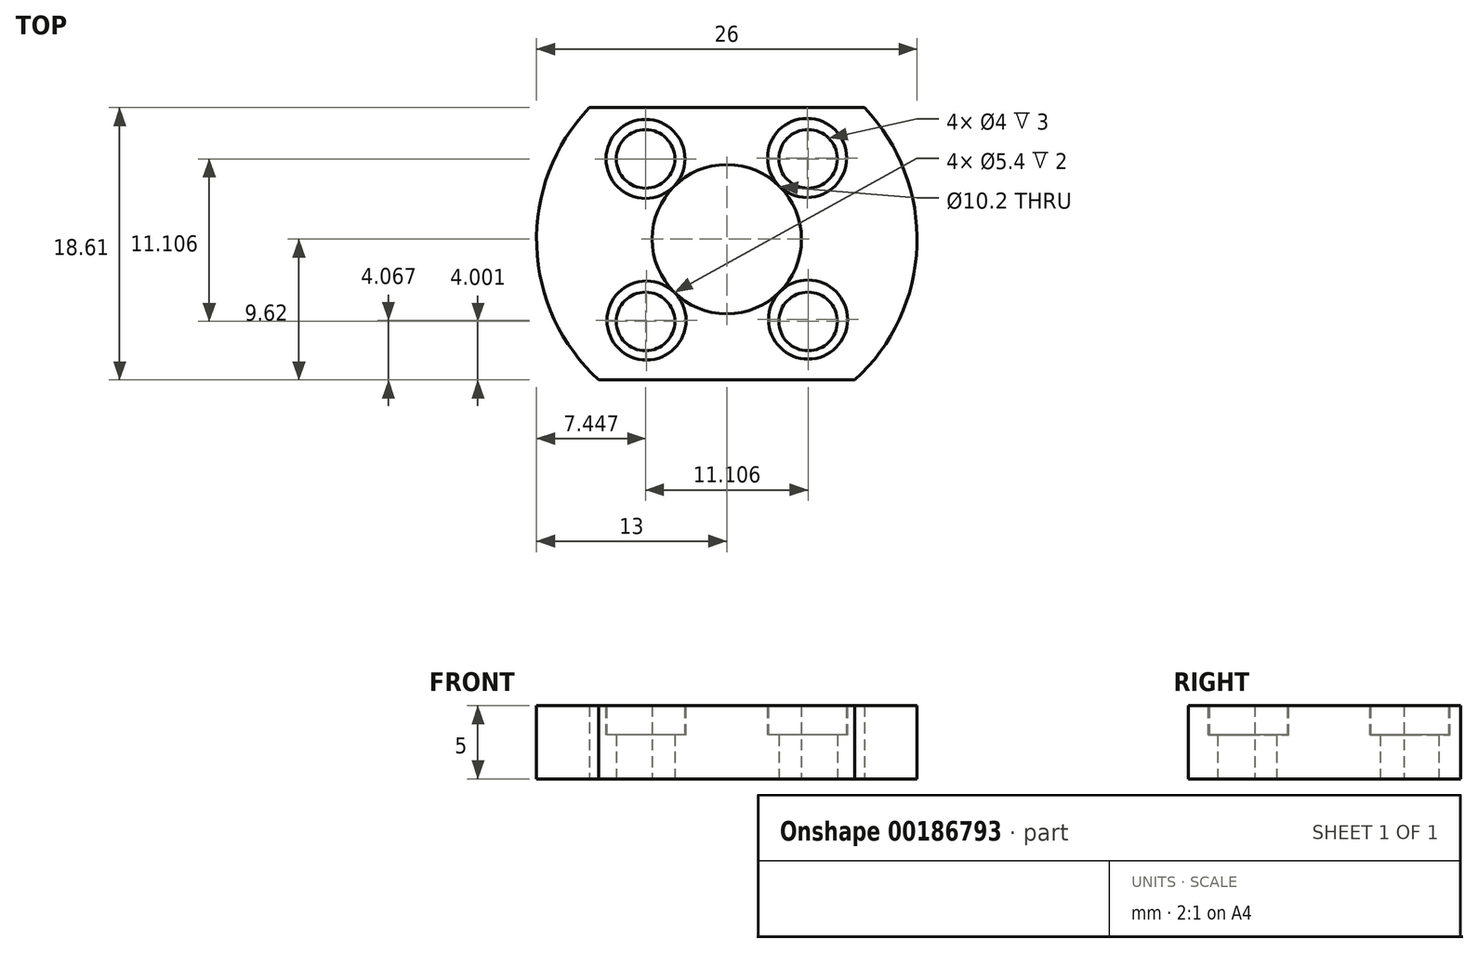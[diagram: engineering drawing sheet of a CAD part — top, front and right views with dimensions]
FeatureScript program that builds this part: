
annotation { "Feature Type Name" : "Feature", "Feature Type Description" : "" }
export const myFeature = defineFeature(function(context is Context, id is Id, definition is map)
    precondition{}
    {
        {
            var Q0;
            Q0=qCreatedBy(makeId("Top.planeOp"),FACE);
            var sketch = newSketch(context, id + "F0", { "sketchPlane" : qUnion([Q0])});
            skCircle(sketch, "E0", {"center": v(0, 0) * mm, "radius": 5.1 * mm});
            skCircle(sketch, "E1", {"center": v(-5.55, -5.62) * mm, "radius": 2 * mm});
            skCircle(sketch, "E2.1.0", {"center": v(5.55, -5.62) * mm, "radius": 2 * mm});
            skCircle(sketch, "E2.2.0", {"center": v(5.55, 5.49) * mm, "radius": 2 * mm});
            skCircle(sketch, "E2.3.0", {"center": v(-5.55, 5.49) * mm, "radius": 2 * mm});
            skPoint(sketch, "E2.center", {"position": v(0, -0.07) * mm});
            skArc(sketch, "E3", {"start": v(8.74, -9.62) * mm, "mid": v(13, -0.45) * mm, "end": v(9.4, 8.99) * mm});
            skLineSegment(sketch, "E4", {"start": v(-8.74, -9.62) * mm, "end": v(8.74, -9.62) * mm});
            skLineSegment(sketch, "E5", {"start": v(-9.4, 8.99) * mm, "end": v(9.4, 8.99) * mm});
            skArc(sketch, "E6.trimOffspring", {"start": v(-9.4, 8.99) * mm, "mid": v(-13, -0.45) * mm, "end": v(-8.74, -9.62) * mm});
            skSolve(sketch);
        }
        {
            var Q0;
            Q0=makeQuery(id+"F0.imprint","IMPRINT",FACE,{"disambiguationData":[TD([[makeQuery(id+"F0.imprint","IMPRINT",EDGE,{"derivedFrom":sQuery(id+"F0.wireOp",EDGE,"E0")}),-1.0]])]});
            extrude(context, id + "F1", {"entities" : qUnion([Q0]), "depth" : 5 * mm});
        }
        {
            var Q0;
            Q0=makeQuery(id+"F1.opExtrude","CAP_FACE",FACE,{"disambiguationData":[OSD([sQuery(id+"F0.wireOp",EDGE,"E0"),sQuery(id+"F0.wireOp",EDGE,"E1"),sQuery(id+"F0.wireOp",EDGE,"E2.1.0"),sQuery(id+"F0.wireOp",EDGE,"E2.2.0"),sQuery(id+"F0.wireOp",EDGE,"E2.3.0"),sQuery(id+"F0.wireOp",EDGE,"E3"),sQuery(id+"F0.wireOp",EDGE,"E4")])],"isStart":false});
            var sketch = newSketch(context, id + "F2", { "sketchPlane" : qUnion([Q0])});
            skCircle(sketch, "E7", {"center": v(-5.55, 5.49) * mm, "radius": 2.7 * mm});
            skCircle(sketch, "E8.1.0", {"center": v(-5.49, -5.55) * mm, "radius": 2.7 * mm});
            skCircle(sketch, "E8.2.0", {"center": v(5.55, -5.49) * mm, "radius": 2.7 * mm});
            skCircle(sketch, "E8.3.0", {"center": v(5.49, 5.55) * mm, "radius": 2.7 * mm});
            skPoint(sketch, "E8.center", {"position": v(0, 0) * mm});
            skSolve(sketch);
        }
        {
            var Q0;
            Q0=makeQuery(id+"F2.imprint","IMPRINT",FACE,{"disambiguationData":[TD([[makeQuery(id+"F2.imprint","IMPRINT",EDGE,{"derivedFrom":sQuery(id+"F2.wireOp",EDGE,"E7")}),1.0]])]});
            var Q1;
            Q1=makeQuery(id+"F2.imprint","IMPRINT",FACE,{"disambiguationData":[TD([[makeQuery(id+"F2.imprint","IMPRINT",EDGE,{"derivedFrom":sQuery(id+"F2.wireOp",EDGE,"E8.3.0")}),1.0]])]});
            var Q2;
            Q2=makeQuery(id+"F2.imprint","IMPRINT",FACE,{"disambiguationData":[TD([[makeQuery(id+"F2.imprint","IMPRINT",EDGE,{"derivedFrom":sQuery(id+"F2.wireOp",EDGE,"E8.2.0")}),1.0]])]});
            var Q3;
            Q3=makeQuery(id+"F2.imprint","IMPRINT",FACE,{"disambiguationData":[TD([[makeQuery(id+"F2.imprint","IMPRINT",EDGE,{"derivedFrom":sQuery(id+"F2.wireOp",EDGE,"E8.1.0")}),1.0]])]});
            extrude(context, id + "F3", {"entities" : qUnion([Q0, Q1, Q2, Q3]), "operationType" : NewBodyOperationType.REMOVE, "oppositeDirection" : true, "depth" : 2 * mm});
        }
    });
